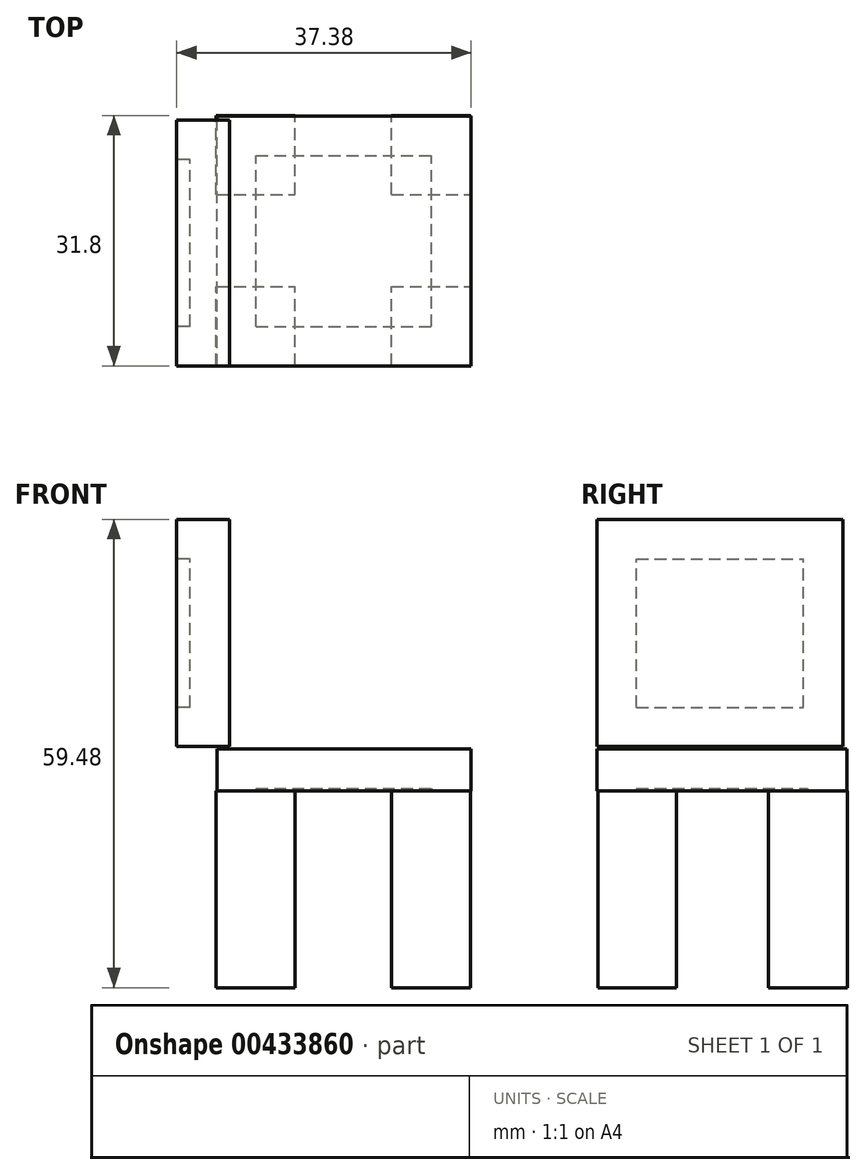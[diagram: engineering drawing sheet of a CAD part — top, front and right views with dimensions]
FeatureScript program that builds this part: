
annotation { "Feature Type Name" : "Feature", "Feature Type Description" : "" }
export const myFeature = defineFeature(function(context is Context, id is Id, definition is map)
    precondition{}
    {
        {
            var Q0;
            Q0=qCreatedBy(makeId("Top.planeOp"),FACE);
            var sketch = newSketch(context, id + "F0", { "sketchPlane" : qUnion([Q0])});
            skLineSegment(sketch, "E0.bottom", {"start": v(5, 5) * mm, "end": v(15, 5) * mm});
            skLineSegment(sketch, "E0.top", {"start": v(5, 15) * mm, "end": v(15, 15) * mm});
            skLineSegment(sketch, "E0.left", {"start": v(5, 5) * mm, "end": v(5, 15) * mm});
            skLineSegment(sketch, "E0.right", {"start": v(15, 5) * mm, "end": v(15, 15) * mm});
            skLineSegment(sketch, "E1.0.1.0", {"start": v(5, 36.7) * mm, "end": v(15, 36.7) * mm});
            skLineSegment(sketch, "E1.0.1.1", {"start": v(15, 26.7) * mm, "end": v(15, 36.7) * mm});
            skLineSegment(sketch, "E1.0.1.2", {"start": v(5, 26.7) * mm, "end": v(15, 26.7) * mm});
            skLineSegment(sketch, "E1.0.1.3", {"start": v(5, 26.7) * mm, "end": v(5, 36.7) * mm});
            skLineSegment(sketch, "E1.1.0.0", {"start": v(27.3, 15) * mm, "end": v(37.3, 15) * mm});
            skLineSegment(sketch, "E1.1.0.1", {"start": v(37.3, 5) * mm, "end": v(37.3, 15) * mm});
            skLineSegment(sketch, "E1.1.0.2", {"start": v(27.3, 5) * mm, "end": v(37.3, 5) * mm});
            skLineSegment(sketch, "E1.1.0.3", {"start": v(27.3, 5) * mm, "end": v(27.3, 15) * mm});
            skLineSegment(sketch, "E1.1.1.0", {"start": v(27.3, 36.7) * mm, "end": v(37.3, 36.7) * mm});
            skLineSegment(sketch, "E1.1.1.1", {"start": v(37.3, 26.7) * mm, "end": v(37.3, 36.7) * mm});
            skLineSegment(sketch, "E1.1.1.2", {"start": v(27.3, 26.7) * mm, "end": v(37.3, 26.7) * mm});
            skLineSegment(sketch, "E1.1.1.3", {"start": v(27.3, 26.7) * mm, "end": v(27.3, 36.7) * mm});
            skLineSegment(sketch, "E1.direction1", {"start": v(5, 15) * mm, "end": v(27.3, 15) * mm, "construction": true});
            skLineSegment(sketch, "E1.direction2", {"start": v(5, 15) * mm, "end": v(5, 36.7) * mm, "construction": true});
            skSolve(sketch);
        }
        {
            var Q0;
            Q0 = qSketchRegion(id + "F0", true);
            extrude(context, id + "F1", {"entities" : qUnion([Q0]), "oppositeDirection" : true, "depth" : 25 * mm});
        }
        {
            var Q0;
            Q0=qCreatedBy(makeId("Top.planeOp"),FACE);
            var sketch = newSketch(context, id + "F2", { "sketchPlane" : qUnion([Q0])});
            skLineSegment(sketch, "E2.bottom", {"start": v(5.08, 4.9) * mm, "end": v(37.38, 4.9) * mm});
            skLineSegment(sketch, "E2.top", {"start": v(5.08, 36.65) * mm, "end": v(37.38, 36.65) * mm});
            skLineSegment(sketch, "E2.left", {"start": v(5.08, 4.9) * mm, "end": v(5.08, 36.65) * mm});
            skLineSegment(sketch, "E2.right", {"start": v(37.38, 4.9) * mm, "end": v(37.38, 36.65) * mm});
            skSolve(sketch);
        }
        {
            var Q0;
            Q0=makeQuery(id+"F2.imprint","IMPRINT",FACE,{"disambiguationData":[TD([[makeQuery(id+"F2.imprint","IMPRINT",EDGE,{"derivedFrom":sQuery(id+"F2.wireOp",EDGE,"E2.bottom")}),1.0]])]});
            extrude(context, id + "F3", {"entities" : qUnion([Q0]), "depth" : 5.3 * mm});
        }
        {
            var Q0;
            Q0=qCreatedBy(makeId("Right.planeOp"),FACE);
            var sketch = newSketch(context, id + "F4", { "sketchPlane" : qUnion([Q0])});
            skLineSegment(sketch, "E3.bottom", {"start": v(4.9, 5.63) * mm, "end": v(36.1, 5.63) * mm});
            skLineSegment(sketch, "E3.top", {"start": v(4.9, 34.48) * mm, "end": v(36.1, 34.48) * mm});
            skLineSegment(sketch, "E3.left", {"start": v(4.9, 5.63) * mm, "end": v(4.9, 34.48) * mm});
            skLineSegment(sketch, "E3.right", {"start": v(36.1, 5.63) * mm, "end": v(36.1, 34.48) * mm});
            skSolve(sketch);
        }
        {
            var Q0;
            Q0=makeQuery(id+"F4.imprint","IMPRINT",FACE,{"disambiguationData":[TD([[makeQuery(id+"F4.imprint","IMPRINT",EDGE,{"derivedFrom":sQuery(id+"F4.wireOp",EDGE,"E3.bottom")}),1.0]])]});
            extrude(context, id + "F5", {"entities" : qUnion([Q0]), "depth" : 6.7 * mm});
        }
        {
            var Q0;
            Q0=makeQuery(id+"F5.opExtrude","CAP_FACE",FACE,{"disambiguationData":[OSD([sQuery(id+"F4.wireOp",EDGE,"E3.bottom"),sQuery(id+"F4.wireOp",EDGE,"E3.top"),sQuery(id+"F4.wireOp",EDGE,"E3.left"),sQuery(id+"F4.wireOp",EDGE,"E3.right")])],"isStart":true});
            shell(context, id + "F6", {"entities" : qUnion([Q0]), "thickness" : 5 * mm});
        }
        {
            var Q0;
            Q0=makeQuery(id+"F3.opExtrude","CAP_FACE",FACE,{"disambiguationData":[OSD([sQuery(id+"F2.wireOp",EDGE,"E2.bottom"),sQuery(id+"F2.wireOp",EDGE,"E2.top"),sQuery(id+"F2.wireOp",EDGE,"E2.left"),sQuery(id+"F2.wireOp",EDGE,"E2.right")])],"isStart":true});
            shell(context, id + "F7", {"entities" : qUnion([Q0]), "thickness" : 5 * mm});
        }
    });
